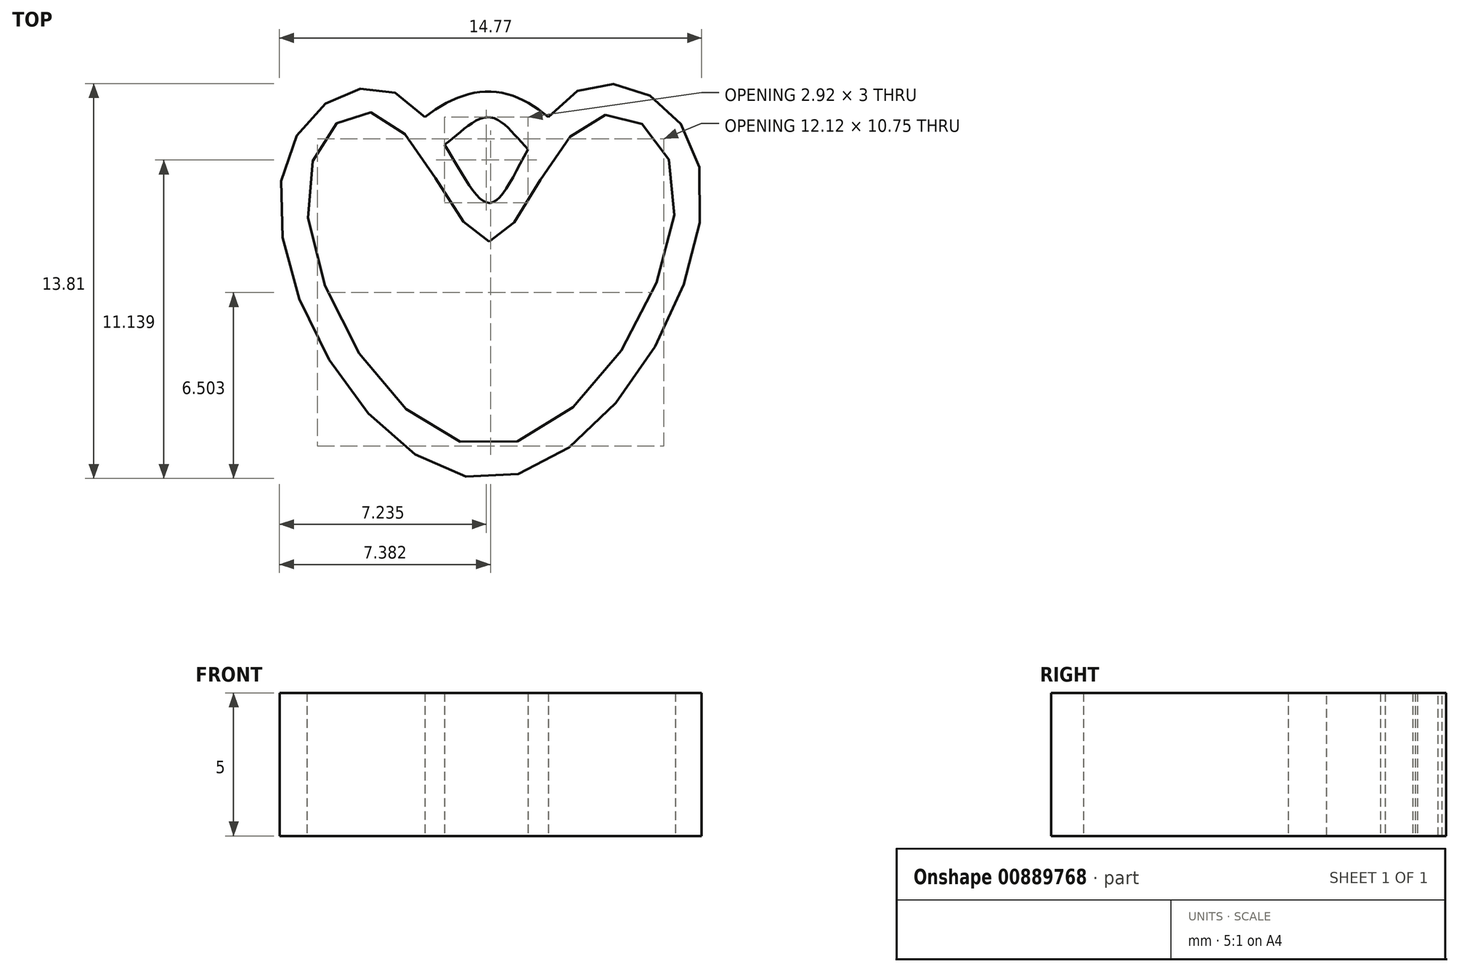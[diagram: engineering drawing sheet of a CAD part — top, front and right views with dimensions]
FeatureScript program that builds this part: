
annotation { "Feature Type Name" : "Feature", "Feature Type Description" : "" }
export const myFeature = defineFeature(function(context is Context, id is Id, definition is map)
    precondition{}
    {
        {
            var Q0;
            Q0=qCreatedBy(makeId("Top.planeOp"),FACE);
            var sketch = newSketch(context, id + "F0", { "sketchPlane" : qUnion([Q0])});
            skFitSpline(sketch, "E0", {"points": [v(0, 4.15) * mm, v(2.9, 7.97) * mm, v(7.32, 5.5) * mm, v(0, -5.5) * mm, v(-7.27, 5) * mm, v(-3.12, 7.91) * mm, v(0, 4.15) * mm]});
            skFitSpline(sketch, "E1", {"points": [v(0, 2.8) * mm, v(3.45, 7) * mm, v(6.46, 4.95) * mm, v(0, -4.36) * mm, v(-6.35, 4.74) * mm, v(-3.66, 7.15) * mm, v(0, 2.8) * mm]});
            skFitSpline(sketch, "E2", {"points": [v(-2.25, 7.15) * mm, v(0, 8.05) * mm, v(2.06, 7.15) * mm], "startDerivative": vector(4.16, 3.28) * mm, "endDerivative": vector(3.84, -3.32) * mm});
            skFitSpline(sketch, "E3", {"points": [v(-1.56, 6.18) * mm, v(0, 7.15) * mm, v(1.35, 6.03) * mm], "startDerivative": vector(3.17, 2.37) * mm, "endDerivative": vector(2.67, -2.7) * mm});
            skSolve(sketch);
        }
        {
            var Q0;
            Q0 = qSketchRegion(id + "F0", true);
            extrude(context, id + "F1", {"entities" : qUnion([Q0]), "depth" : 5 * mm, "offsetDistance" : 25.4 * mm});
        }
        {
            var Q0;
            Q0 = qSketchRegion(id + "F0", true);
            extrude(context, id + "F2", {"entities" : qUnion([Q0]), "operationType" : NewBodyOperationType.ADD, "depth" : 5 * mm, "offsetDistance" : 25.4 * mm});
        }
    });
